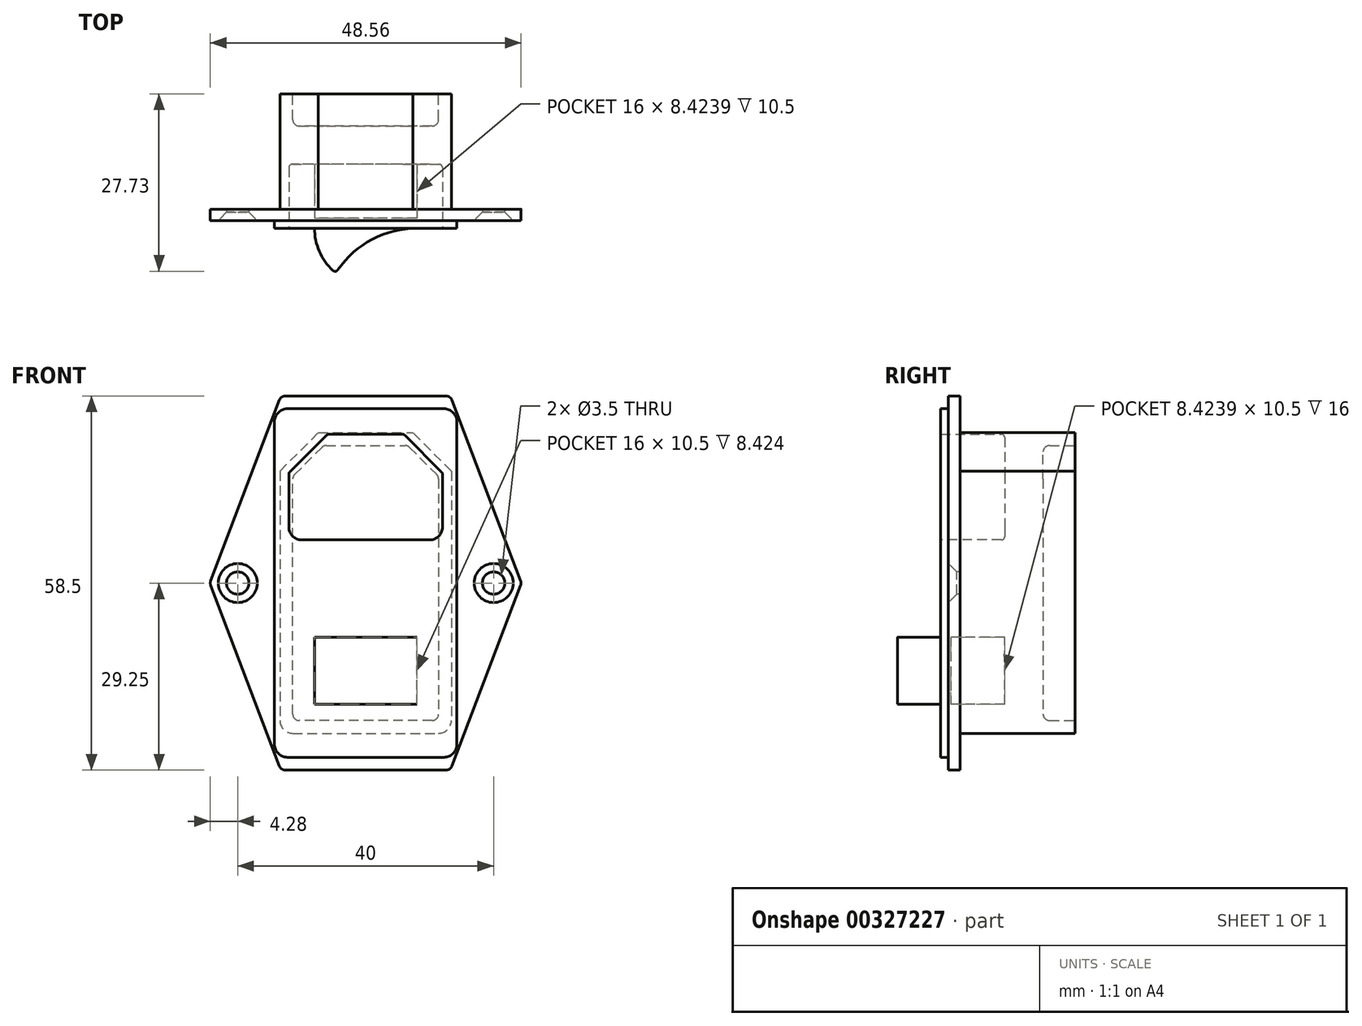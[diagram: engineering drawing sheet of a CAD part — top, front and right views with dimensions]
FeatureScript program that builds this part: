
annotation { "Feature Type Name" : "Feature", "Feature Type Description" : "" }
export const myFeature = defineFeature(function(context is Context, id is Id, definition is map)
    precondition{}
    {
        {
            var Q0;
            Q0=qCreatedBy(makeId("Front.planeOp"),FACE);
            var sketch = newSketch(context, id + "F0", { "sketchPlane" : qUnion([Q0])});
            skLineSegment(sketch, "E0.bottom", {"start": v(-13.4, 23.5) * mm, "end": v(13.4, 23.5) * mm});
            skLineSegment(sketch, "E0.top", {"start": v(-13.4, -23.5) * mm, "end": v(13.4, -23.5) * mm});
            skLineSegment(sketch, "E0.left", {"start": v(-13.4, 23.5) * mm, "end": v(-13.4, -23.5) * mm});
            skLineSegment(sketch, "E0.right", {"start": v(13.4, 23.5) * mm, "end": v(13.4, -23.5) * mm});
            skPoint(sketch, "E0.middle", {"position": v(0, 0) * mm});
            skSolve(sketch);
        }
        {
            var Q0;
            Q0 = qSketchRegion(id + "F0", true);
            extrude(context, id + "F1", {"entities" : qUnion([Q0]), "oppositeDirection" : true, "depth" : 18 * mm});
        }
        {
            var Q0;
            Q0=makeQuery(id+"F1.opExtrude","SWEPT_EDGE",EDGE,{"disambiguationData":[OSD([sQuery(id+"F0.wireOp",EDGE,"E0.bottom"),sQuery(id+"F0.wireOp",EDGE,"E0.left")])]});
            var Q1;
            Q1=makeQuery(id+"F1.opExtrude","SWEPT_EDGE",EDGE,{"disambiguationData":[OSD([sQuery(id+"F0.wireOp",EDGE,"E0.bottom"),sQuery(id+"F0.wireOp",EDGE,"E0.right")])]});
            chamfer(context, id + "F2", {"entities" : qUnion([Q0, Q1]), "width" : 6 * mm, "tangentPropagation" : true});
        }
        {
            var Q0;
            Q0=makeQuery(id+"F1.opExtrude","SWEPT_EDGE",EDGE,{"disambiguationData":[OSD([sQuery(id+"F0.wireOp",EDGE,"E0.top"),sQuery(id+"F0.wireOp",EDGE,"E0.left")])]});
            var Q1;
            Q1=makeQuery(id+"F1.opExtrude","SWEPT_EDGE",EDGE,{"disambiguationData":[OSD([sQuery(id+"F0.wireOp",EDGE,"E0.top"),sQuery(id+"F0.wireOp",EDGE,"E0.right")])]});
            fillet(context, id + "F3", {"entities" : qUnion([Q0, Q1]), "radius" : 2 * mm, "tangentPropagation" : true, "allowEdgeOverflow" : false});
        }
        {
            var Q0;
            Q0=makeQuery(id+"F1.opExtrude","CAP_FACE",FACE,{"disambiguationData":[OSD([sQuery(id+"F0.wireOp",EDGE,"E0.bottom"),sQuery(id+"F0.wireOp",EDGE,"E0.top"),sQuery(id+"F0.wireOp",EDGE,"E0.left"),sQuery(id+"F0.wireOp",EDGE,"E0.right")])],"isStart":false});
            var sketch = newSketch(context, id + "F4", { "sketchPlane" : qUnion([Q0])});
            skLineSegment(sketch, "E1.0.0", {"start": v(-11.4, -23.5) * mm, "end": v(11.4, -23.5) * mm, "construction": true});
            skArc(sketch, "E1.0.1", {"start": v(11.4, -23.5) * mm, "mid": v(12.81, -22.91) * mm, "end": v(13.4, -21.5) * mm, "construction": true});
            skLineSegment(sketch, "E1.0.2", {"start": v(13.4, -21.5) * mm, "end": v(13.4, 17.5) * mm, "construction": true});
            skLineSegment(sketch, "E1.0.3", {"start": v(13.4, 17.5) * mm, "end": v(7.4, 23.5) * mm, "construction": true});
            skLineSegment(sketch, "E1.0.4", {"start": v(7.4, 23.5) * mm, "end": v(-7.4, 23.5) * mm, "construction": true});
            skLineSegment(sketch, "E1.0.5", {"start": v(-7.4, 23.5) * mm, "end": v(-13.4, 17.5) * mm, "construction": true});
            skLineSegment(sketch, "E1.0.6", {"start": v(-13.4, 17.5) * mm, "end": v(-13.4, -21.5) * mm, "construction": true});
            skArc(sketch, "E1.0.7", {"start": v(-13.4, -21.5) * mm, "mid": v(-12.81, -22.91) * mm, "end": v(-11.4, -23.5) * mm, "construction": true});
            skLineSegment(sketch, "E2.0", {"start": v(-11.4, 16.67) * mm, "end": v(-11.4, -21.5) * mm});
            skLineSegment(sketch, "E2.1", {"start": v(11.4, -21.5) * mm, "end": v(11.4, 16.67) * mm});
            skLineSegment(sketch, "E2.2", {"start": v(11.4, 16.67) * mm, "end": v(6.57, 21.5) * mm});
            skLineSegment(sketch, "E2.3", {"start": v(-11.4, -21.5) * mm, "end": v(11.4, -21.5) * mm});
            skLineSegment(sketch, "E2.4", {"start": v(6.57, 21.5) * mm, "end": v(-6.57, 21.5) * mm});
            skLineSegment(sketch, "E2.5", {"start": v(-6.57, 21.5) * mm, "end": v(-11.4, 16.67) * mm});
            skSolve(sketch);
        }
        {
            var Q0;
            Q0 = qSketchRegion(id + "F4", true);
            extrude(context, id + "F5", {"entities" : qUnion([Q0]), "operationType" : NewBodyOperationType.REMOVE, "oppositeDirection" : true, "depth" : 5 * mm});
        }
        {
            var Q0;
            Q0=makeQuery(id+"F5.boolean.opBoolean","COPY",EDGE,{"derivedFrom":makeQuery(id+"F5.opExtrude","SWEPT_EDGE",EDGE,{"disambiguationData":[OSD([sQuery(id+"F4.wireOp",EDGE,"E2.1"),sQuery(id+"F4.wireOp",EDGE,"E2.3")])]})});
            var Q1;
            Q1=makeQuery(id+"F5.boolean.opBoolean","COPY",EDGE,{"derivedFrom":makeQuery(id+"F5.opExtrude","SWEPT_EDGE",EDGE,{"disambiguationData":[OSD([sQuery(id+"F4.wireOp",EDGE,"E2.1"),sQuery(id+"F4.wireOp",EDGE,"E2.2")])]})});
            var Q2;
            Q2=makeQuery(id+"F5.boolean.opBoolean","COPY",EDGE,{"derivedFrom":makeQuery(id+"F5.opExtrude","SWEPT_EDGE",EDGE,{"disambiguationData":[OSD([sQuery(id+"F4.wireOp",EDGE,"E2.2"),sQuery(id+"F4.wireOp",EDGE,"E2.4")])]})});
            var Q3;
            Q3=makeQuery(id+"F5.boolean.opBoolean","COPY",EDGE,{"derivedFrom":makeQuery(id+"F5.opExtrude","SWEPT_EDGE",EDGE,{"disambiguationData":[OSD([sQuery(id+"F4.wireOp",EDGE,"E2.4"),sQuery(id+"F4.wireOp",EDGE,"E2.5")])]})});
            var Q4;
            Q4=makeQuery(id+"F5.boolean.opBoolean","COPY",EDGE,{"derivedFrom":makeQuery(id+"F5.opExtrude","SWEPT_EDGE",EDGE,{"disambiguationData":[OSD([sQuery(id+"F4.wireOp",EDGE,"E2.0"),sQuery(id+"F4.wireOp",EDGE,"E2.5")])]})});
            var Q5;
            Q5=makeQuery(id+"F5.boolean.opBoolean","COPY",EDGE,{"derivedFrom":makeQuery(id+"F5.opExtrude","SWEPT_EDGE",EDGE,{"disambiguationData":[OSD([sQuery(id+"F4.wireOp",EDGE,"E2.0"),sQuery(id+"F4.wireOp",EDGE,"E2.3")])]})});
            var Q6;
            Q6=makeQuery(id+"F5.boolean.opBoolean","COPY",FACE,{"derivedFrom":makeQuery(id+"F5.opExtrude","CAP_FACE",FACE,{"disambiguationData":[OSD([sQuery(id+"F4.wireOp",EDGE,"E2.0"),sQuery(id+"F4.wireOp",EDGE,"E2.1"),sQuery(id+"F4.wireOp",EDGE,"E2.2"),sQuery(id+"F4.wireOp",EDGE,"E2.3"),sQuery(id+"F4.wireOp",EDGE,"E2.4"),sQuery(id+"F4.wireOp",EDGE,"E2.5")])],"isStart":false})});
            fillet(context, id + "F6", {"entities" : qUnion([Q0, Q1, Q2, Q3, Q4, Q5, Q6]), "radius" : 1 * mm, "tangentPropagation" : true, "allowEdgeOverflow" : false});
        }
        {
            var Q0;
            Q0=makeQuery(id+"F1.opExtrude","CAP_FACE",FACE,{"disambiguationData":[OSD([sQuery(id+"F0.wireOp",EDGE,"E0.bottom"),sQuery(id+"F0.wireOp",EDGE,"E0.top"),sQuery(id+"F0.wireOp",EDGE,"E0.left"),sQuery(id+"F0.wireOp",EDGE,"E0.right")])],"isStart":true});
            var sketch = newSketch(context, id + "F7", { "sketchPlane" : qUnion([Q0])});
            skLineSegment(sketch, "E3", {"start": v(0, 23.5) * mm, "end": v(0, -23.5) * mm, "construction": true});
            skPoint(sketch, "E4", {"position": v(0, 0) * mm});
            skLineSegment(sketch, "E5.bottom", {"start": v(-14.25, 27.25) * mm, "end": v(14.25, 27.25) * mm});
            skLineSegment(sketch, "E5.top", {"start": v(-14.25, -27.25) * mm, "end": v(14.25, -27.25) * mm});
            skLineSegment(sketch, "E5.left", {"start": v(-14.25, 27.25) * mm, "end": v(-14.25, -27.25) * mm});
            skLineSegment(sketch, "E5.right", {"start": v(14.25, 27.25) * mm, "end": v(14.25, -27.25) * mm});
            skSolve(sketch);
        }
        {
            var Q0;
            Q0 = qSketchRegion(id + "F7", true);
            extrude(context, id + "F8", {"entities" : qUnion([Q0]), "operationType" : NewBodyOperationType.ADD, "depth" : 3 * mm});
        }
        {
            var Q0;
            Q0=makeQuery(id+"F8.opExtrude","CAP_FACE",FACE,{"disambiguationData":[OSD([sQuery(id+"F7.wireOp",EDGE,"E5.bottom"),sQuery(id+"F7.wireOp",EDGE,"E5.top"),sQuery(id+"F7.wireOp",EDGE,"E5.left"),sQuery(id+"F7.wireOp",EDGE,"E5.right")])],"isStart":false});
            cPlane(context, id + "F9", {"entities" : qUnion([Q0]), "cplaneType" : CPlaneType.OFFSET, "offset" : 1.2 * mm, "oppositeDirection" : true, "width" : 150 * mm, "height" : 150 * mm});
        }
        {
            var Q0;
            Q0=qCreatedBy(id+"F9.planeOp",FACE);
            var sketch = newSketch(context, id + "F10", { "sketchPlane" : qUnion([Q0])});
            skLineSegment(sketch, "E6.0.0", {"start": v(-14.25, 27.25) * mm, "end": v(-14.25, -27.25) * mm, "construction": true});
            skLineSegment(sketch, "E6.0.1", {"start": v(-14.25, -27.25) * mm, "end": v(14.25, -27.25) * mm, "construction": true});
            skLineSegment(sketch, "E6.0.2", {"start": v(14.25, -27.25) * mm, "end": v(14.25, 27.25) * mm, "construction": true});
            skLineSegment(sketch, "E6.0.3", {"start": v(14.25, 27.25) * mm, "end": v(-14.25, 27.25) * mm, "construction": true});
            skPoint(sketch, "E7", {"position": v(0, 0) * mm});
            skPoint(sketch, "E7.positionSnap0", {"position": v(-14.25, 0) * mm});
            skPoint(sketch, "E7.positionSnap1", {"position": v(0, 27.25) * mm});
            skPoint(sketch, "E8", {"position": v(-20, 0) * mm});
            skPoint(sketch, "E9", {"position": v(20, 0) * mm});
            skCircle(sketch, "E10", {"center": v(-20, 0) * mm, "radius": 1.75 * mm});
            skCircle(sketch, "E11", {"center": v(20, 0) * mm, "radius": 1.75 * mm});
            skLineSegment(sketch, "E12.0", {"start": v(13.25, 29.25) * mm, "end": v(-13.25, 29.25) * mm});
            skLineSegment(sketch, "E13.0", {"start": v(-13.25, -29.25) * mm, "end": v(13.25, -29.25) * mm});
            skPoint(sketch, "E14", {"position": v(-24.35, 0) * mm});
            skPoint(sketch, "E15", {"position": v(24.35, 0) * mm});
            skPoint(sketch, "E15.positionSnap0", {"position": v(14.25, 0) * mm});
            skLineSegment(sketch, "E16", {"start": v(-13.25, -29.25) * mm, "end": v(-13.25, 30.88) * mm, "construction": true});
            skLineSegment(sketch, "E17", {"start": v(13.25, -29.25) * mm, "end": v(13.25, 30.88) * mm, "construction": true});
            skPoint(sketch, "E18.orphan", {"position": v(-13.25, 27.25) * mm});
            skPoint(sketch, "E19.orphan", {"position": v(13.25, 27.25) * mm});
            skLineSegment(sketch, "E20", {"start": v(-13.25, -29.25) * mm, "end": v(-24.35, 0) * mm});
            skLineSegment(sketch, "E21", {"start": v(-24.35, 0) * mm, "end": v(-13.25, 29.25) * mm});
            skLineSegment(sketch, "E22", {"start": v(13.25, 29.25) * mm, "end": v(24.35, 0) * mm});
            skLineSegment(sketch, "E23", {"start": v(24.35, 0) * mm, "end": v(13.25, -29.25) * mm});
            skSolve(sketch);
        }
        {
            var Q0;
            Q0 = qSketchRegion(id + "F10", true);
            extrude(context, id + "F11", {"entities" : qUnion([Q0]), "operationType" : NewBodyOperationType.ADD, "oppositeDirection" : true, "depth" : 1.8 * mm});
        }
        {
            var Q0;
            Q0=makeQuery(id+"F8.opExtrude","SWEPT_EDGE",EDGE,{"disambiguationData":[OSD([sQuery(id+"F7.wireOp",EDGE,"E5.bottom"),sQuery(id+"F7.wireOp",EDGE,"E5.right")])]});
            var Q1;
            Q1=makeQuery(id+"F8.opExtrude","SWEPT_EDGE",EDGE,{"disambiguationData":[OSD([sQuery(id+"F7.wireOp",EDGE,"E5.bottom"),sQuery(id+"F7.wireOp",EDGE,"E5.left")])]});
            var Q2;
            Q2=makeQuery(id+"F8.opExtrude","SWEPT_EDGE",EDGE,{"disambiguationData":[OSD([sQuery(id+"F7.wireOp",EDGE,"E5.top"),sQuery(id+"F7.wireOp",EDGE,"E5.right")])]});
            var Q3;
            Q3=makeQuery(id+"F8.opExtrude","SWEPT_EDGE",EDGE,{"disambiguationData":[OSD([sQuery(id+"F7.wireOp",EDGE,"E5.top"),sQuery(id+"F7.wireOp",EDGE,"E5.left")])]});
            fillet(context, id + "F12", {"entities" : qUnion([Q0, Q1, Q2, Q3]), "radius" : 2 * mm, "tangentPropagation" : true, "allowEdgeOverflow" : false});
        }
        {
            var Q0;
            Q0=makeQuery(id+"F11.opExtrude","SWEPT_EDGE",EDGE,{"disambiguationData":[OSD([sQuery(id+"F10.wireOp",EDGE,"E12.0"),sQuery(id+"F10.wireOp",EDGE,"E21")])]});
            var Q1;
            Q1=makeQuery(id+"F11.opExtrude","SWEPT_EDGE",EDGE,{"disambiguationData":[OSD([sQuery(id+"F10.wireOp",EDGE,"E12.0"),sQuery(id+"F10.wireOp",EDGE,"E22")])]});
            var Q2;
            Q2=makeQuery(id+"F11.opExtrude","SWEPT_EDGE",EDGE,{"disambiguationData":[OSD([sQuery(id+"F10.wireOp",EDGE,"E20"),sQuery(id+"F10.wireOp",EDGE,"E21")])]});
            var Q3;
            Q3=makeQuery(id+"F11.opExtrude","SWEPT_EDGE",EDGE,{"disambiguationData":[OSD([sQuery(id+"F10.wireOp",EDGE,"E13.0"),sQuery(id+"F10.wireOp",EDGE,"E20")])]});
            var Q4;
            Q4=makeQuery(id+"F11.opExtrude","SWEPT_EDGE",EDGE,{"disambiguationData":[OSD([sQuery(id+"F10.wireOp",EDGE,"E13.0"),sQuery(id+"F10.wireOp",EDGE,"E23")])]});
            var Q5;
            Q5=makeQuery(id+"F11.opExtrude","SWEPT_EDGE",EDGE,{"disambiguationData":[OSD([sQuery(id+"F10.wireOp",EDGE,"E22"),sQuery(id+"F10.wireOp",EDGE,"E23")])]});
            fillet(context, id + "F13", {"entities" : qUnion([Q0, Q1, Q2, Q3, Q4, Q5]), "radius" : 1 * mm, "tangentPropagation" : true, "allowEdgeOverflow" : false});
        }
        {
            var Q0;
            Q0=makeQuery(id+"F11.opExtrude","CAP_EDGE",EDGE,{"disambiguationData":[OSD([sQuery(id+"F10.wireOp",EDGE,"E10")])],"isStart":true});
            var Q1;
            Q1=makeQuery(id+"F11.opExtrude","CAP_EDGE",EDGE,{"disambiguationData":[OSD([sQuery(id+"F10.wireOp",EDGE,"E11")])],"isStart":true});
            chamfer(context, id + "F14", {"entities" : qUnion([Q0, Q1]), "width" : 1.3 * mm, "tangentPropagation" : true});
        }
        {
            var Q0;
            Q0=makeQuery(id+"F8.opExtrude","CAP_FACE",FACE,{"disambiguationData":[OSD([sQuery(id+"F7.wireOp",EDGE,"E5.bottom"),sQuery(id+"F7.wireOp",EDGE,"E5.top"),sQuery(id+"F7.wireOp",EDGE,"E5.left"),sQuery(id+"F7.wireOp",EDGE,"E5.right")])],"isStart":false});
            var sketch = newSketch(context, id + "F15", { "sketchPlane" : qUnion([Q0])});
            skLineSegment(sketch, "E24.0", {"start": v(-12.25, 27.25) * mm, "end": v(12.25, 27.25) * mm, "construction": true});
            skLineSegment(sketch, "E25.0", {"start": v(-12, 23.25) * mm, "end": v(12, 23.25) * mm, "construction": true});
            skPoint(sketch, "E26", {"position": v(0, 23.25) * mm});
            skPoint(sketch, "E27", {"position": v(0, 15) * mm});
            skLineSegment(sketch, "E28.bottom", {"start": v(12, 23.25) * mm, "end": v(-12, 23.25) * mm});
            skLineSegment(sketch, "E28.top", {"start": v(12, 6.75) * mm, "end": v(-12, 6.75) * mm});
            skLineSegment(sketch, "E28.left", {"start": v(12, 23.25) * mm, "end": v(12, 6.75) * mm});
            skLineSegment(sketch, "E28.right", {"start": v(-12, 23.25) * mm, "end": v(-12, 6.75) * mm});
            skSolve(sketch);
        }
        {
            var Q0;
            Q0 = qSketchRegion(id + "F15", true);
            extrude(context, id + "F16", {"entities" : qUnion([Q0]), "oppositeDirection" : true, "depth" : 10 * mm});
        }
        {
            var Q0;
            Q0=makeQuery(id+"F16.opExtrude","SWEPT_EDGE",EDGE,{"disambiguationData":[OSD([sQuery(id+"F15.wireOp",EDGE,"E28.bottom"),sQuery(id+"F15.wireOp",EDGE,"E28.left")])]});
            var Q1;
            Q1=makeQuery(id+"F16.opExtrude","SWEPT_EDGE",EDGE,{"disambiguationData":[OSD([sQuery(id+"F15.wireOp",EDGE,"E28.bottom"),sQuery(id+"F15.wireOp",EDGE,"E28.right")])]});
            chamfer(context, id + "F17", {"entities" : qUnion([Q0, Q1]), "width" : 6 * mm, "tangentPropagation" : true});
        }
        {
            var Q0;
            Q0=makeQuery(id+"F16.opExtrude","SWEPT_BODY",BODY,{"disambiguationData":[OSD([sQuery(id+"F15.wireOp",EDGE,"E28.bottom"),sQuery(id+"F15.wireOp",EDGE,"E28.top"),sQuery(id+"F15.wireOp",EDGE,"E28.left"),sQuery(id+"F15.wireOp",EDGE,"E28.right")])]});
            var Q1;
            Q1=makeQuery(id+"F1.opExtrude","SWEPT_BODY",BODY,{"disambiguationData":[OSD([sQuery(id+"F0.wireOp",EDGE,"E0.bottom"),sQuery(id+"F0.wireOp",EDGE,"E0.top"),sQuery(id+"F0.wireOp",EDGE,"E0.left"),sQuery(id+"F0.wireOp",EDGE,"E0.right")])]});
            booleanBodies(context, id + "F18", {"operationType" : BooleanOperationType.SUBTRACTION, "tools" : qUnion([Q0]), "targets" : qUnion([Q1])});
        }
        {
            var Q0;
            Q0=makeQuery(id+"F18.opBoolean","COPY",EDGE,{"derivedFrom":makeQuery(id+"F16.opExtrude","SWEPT_EDGE",EDGE,{"disambiguationData":[OSD([sQuery(id+"F15.wireOp",EDGE,"E28.top"),sQuery(id+"F15.wireOp",EDGE,"E28.right")])]})});
            var Q1;
            Q1=makeQuery(id+"F18.opBoolean","COPY",EDGE,{"derivedFrom":makeQuery(id+"F16.opExtrude","SWEPT_EDGE",EDGE,{"disambiguationData":[OSD([sQuery(id+"F15.wireOp",EDGE,"E28.top"),sQuery(id+"F15.wireOp",EDGE,"E28.left")])]})});
            fillet(context, id + "F19", {"entities" : qUnion([Q0, Q1]), "radius" : 2 * mm, "tangentPropagation" : true, "allowEdgeOverflow" : false});
        }
        {
            var Q0;
            {var subQ0=sQuery(id+"F15.wireOp",EDGE,"E28.left");Q0=makeQuery(id+"F18.opBoolean","COPY",EDGE,{"derivedFrom":makeQuery(id+"F17.opChamfer","BLEND_EDGE",EDGE,{"blendedFrom":[makeQuery(id+"F16.opExtrude","SWEPT_EDGE",EDGE,{"disambiguationData":[OSD([sQuery(id+"F15.wireOp",EDGE,"E28.bottom"),subQ0])]}),makeQuery(id+"F16.opExtrude","SWEPT_FACE",FACE,{"disambiguationData":[OSD([subQ0])]})],"blendedInto":[makeQuery(id+"F16.opExtrude","SWEPT_FACE",FACE,{"disambiguationData":[OSD([subQ0])]})]})});}
            var Q1;
            {var subQ0=sQuery(id+"F15.wireOp",EDGE,"E28.bottom");Q1=makeQuery(id+"F18.opBoolean","COPY",EDGE,{"derivedFrom":makeQuery(id+"F17.opChamfer","BLEND_EDGE",EDGE,{"blendedFrom":[makeQuery(id+"F16.opExtrude","SWEPT_EDGE",EDGE,{"disambiguationData":[OSD([subQ0,sQuery(id+"F15.wireOp",EDGE,"E28.left")])]}),makeQuery(id+"F16.opExtrude","SWEPT_FACE",FACE,{"disambiguationData":[OSD([subQ0])]})],"blendedInto":[makeQuery(id+"F16.opExtrude","SWEPT_FACE",FACE,{"disambiguationData":[OSD([subQ0])]})]})});}
            var Q2;
            {var subQ0=sQuery(id+"F15.wireOp",EDGE,"E28.right");Q2=makeQuery(id+"F18.opBoolean","COPY",EDGE,{"derivedFrom":makeQuery(id+"F17.opChamfer","BLEND_EDGE",EDGE,{"blendedFrom":[makeQuery(id+"F16.opExtrude","SWEPT_EDGE",EDGE,{"disambiguationData":[OSD([sQuery(id+"F15.wireOp",EDGE,"E28.bottom"),subQ0])]}),makeQuery(id+"F16.opExtrude","SWEPT_FACE",FACE,{"disambiguationData":[OSD([subQ0])]})],"blendedInto":[makeQuery(id+"F16.opExtrude","SWEPT_FACE",FACE,{"disambiguationData":[OSD([subQ0])]})]})});}
            var Q3;
            {var subQ0=sQuery(id+"F15.wireOp",EDGE,"E28.bottom");Q3=makeQuery(id+"F18.opBoolean","COPY",EDGE,{"derivedFrom":makeQuery(id+"F17.opChamfer","BLEND_EDGE",EDGE,{"blendedFrom":[makeQuery(id+"F16.opExtrude","SWEPT_EDGE",EDGE,{"disambiguationData":[OSD([subQ0,sQuery(id+"F15.wireOp",EDGE,"E28.right")])]}),makeQuery(id+"F16.opExtrude","SWEPT_FACE",FACE,{"disambiguationData":[OSD([subQ0])]})],"blendedInto":[makeQuery(id+"F16.opExtrude","SWEPT_FACE",FACE,{"disambiguationData":[OSD([subQ0])]})]})});}
            var Q4;
            Q4=makeQuery(id+"F18.opBoolean","COPY",FACE,{"derivedFrom":makeQuery(id+"F16.opExtrude","CAP_FACE",FACE,{"disambiguationData":[OSD([sQuery(id+"F15.wireOp",EDGE,"E28.bottom"),sQuery(id+"F15.wireOp",EDGE,"E28.top"),sQuery(id+"F15.wireOp",EDGE,"E28.left"),sQuery(id+"F15.wireOp",EDGE,"E28.right")])],"isStart":false})});
            fillet(context, id + "F20", {"entities" : qUnion([Q0, Q1, Q2, Q3, Q4]), "radius" : .5 * mm, "tangentPropagation" : true, "allowEdgeOverflow" : false});
        }
        {
            var Q0;
            Q0=makeQuery(id+"F8.opExtrude","CAP_FACE",FACE,{"disambiguationData":[OSD([sQuery(id+"F7.wireOp",EDGE,"E5.bottom"),sQuery(id+"F7.wireOp",EDGE,"E5.top"),sQuery(id+"F7.wireOp",EDGE,"E5.left"),sQuery(id+"F7.wireOp",EDGE,"E5.right")])],"isStart":false});
            var sketch = newSketch(context, id + "F21", { "sketchPlane" : qUnion([Q0])});
            skLineSegment(sketch, "E29.0", {"start": v(-12.25, -27.25) * mm, "end": v(12.25, -27.25) * mm, "construction": true});
            skLineSegment(sketch, "E30.0", {"start": v(-12.25, -18.95) * mm, "end": v(12.25, -18.95) * mm, "construction": true});
            skPoint(sketch, "E31", {"position": v(0, -18.95) * mm});
            skPoint(sketch, "E32", {"position": v(0, -13.7) * mm});
            skLineSegment(sketch, "E33.bottom", {"start": v(8, -18.95) * mm, "end": v(-8, -18.95) * mm});
            skLineSegment(sketch, "E33.top", {"start": v(8, -8.45) * mm, "end": v(-8, -8.45) * mm});
            skLineSegment(sketch, "E33.left", {"start": v(8, -18.95) * mm, "end": v(8, -8.45) * mm});
            skLineSegment(sketch, "E33.right", {"start": v(-8, -18.95) * mm, "end": v(-8, -8.45) * mm});
            skSolve(sketch);
        }
        {
            var Q0;
            Q0 = qSketchRegion(id + "F21", true);
            extrude(context, id + "F22", {"entities" : qUnion([Q0]), "operationType" : NewBodyOperationType.REMOVE, "oppositeDirection" : true, "depth" : 10 * mm});
        }
        {
            var Q0;
            Q0=makeQuery(id+"F22.boolean.opBoolean","COPY",FACE,{"derivedFrom":makeQuery(id+"F22.opExtrude","SWEPT_FACE",FACE,{"disambiguationData":[OSD([sQuery(id+"F21.wireOp",EDGE,"E33.bottom")])]})});
            var sketch = newSketch(context, id + "F23", { "sketchPlane" : qUnion([Q0])});
            skPoint(sketch, "E34.0", {"position": v(8, -3) * mm});
            skPoint(sketch, "E35.0", {"position": v(-8, -3) * mm});
            skArc(sketch, "E36", {"start": v(8, -3) * mm, "mid": v(0.77, -4.86) * mm, "end": v(-4.66, -9.99) * mm});
            skArc(sketch, "E37", {"start": v(-8, -3) * mm, "mid": v(-7.12, -6.87) * mm, "end": v(-4.66, -9.99) * mm});
            skLineSegment(sketch, "E38", {"start": v(8, -3) * mm, "end": v(8, -1.42) * mm});
            skLineSegment(sketch, "E39", {"start": v(8, -1.42) * mm, "end": v(-8, -1.42) * mm});
            skLineSegment(sketch, "E40", {"start": v(-8, -1.42) * mm, "end": v(-8, -3) * mm});
            skSolve(sketch);
        }
        {
            var Q0;
            Q0 = qSketchRegion(id + "F23", true);
            var Q1;
            Q1=makeQuery(id+"F22.boolean.opBoolean","COPY",FACE,{"derivedFrom":makeQuery(id+"F22.opExtrude","SWEPT_FACE",FACE,{"disambiguationData":[OSD([sQuery(id+"F21.wireOp",EDGE,"E33.top")])]})});
            extrude(context, id + "F24", {"entities" : qUnion([Q0]), "operationType" : NewBodyOperationType.ADD, "endBound" : BoundingType.UP_TO_SURFACE, "endBoundEntityFace" : qUnion([Q1]), "depth" : 25 * mm});
        }
        {
            var Q0;
            Q0=makeQuery(id+"F24.opExtrude","SWEPT_EDGE",EDGE,{"disambiguationData":[OSD([sQuery(id+"F23.wireOp",EDGE,"E36"),sQuery(id+"F23.wireOp",EDGE,"E37")])]});
            fillet(context, id + "F25", {"entities" : qUnion([Q0]), "radius" : .5 * mm, "tangentPropagation" : true, "allowEdgeOverflow" : false});
        }
    });
